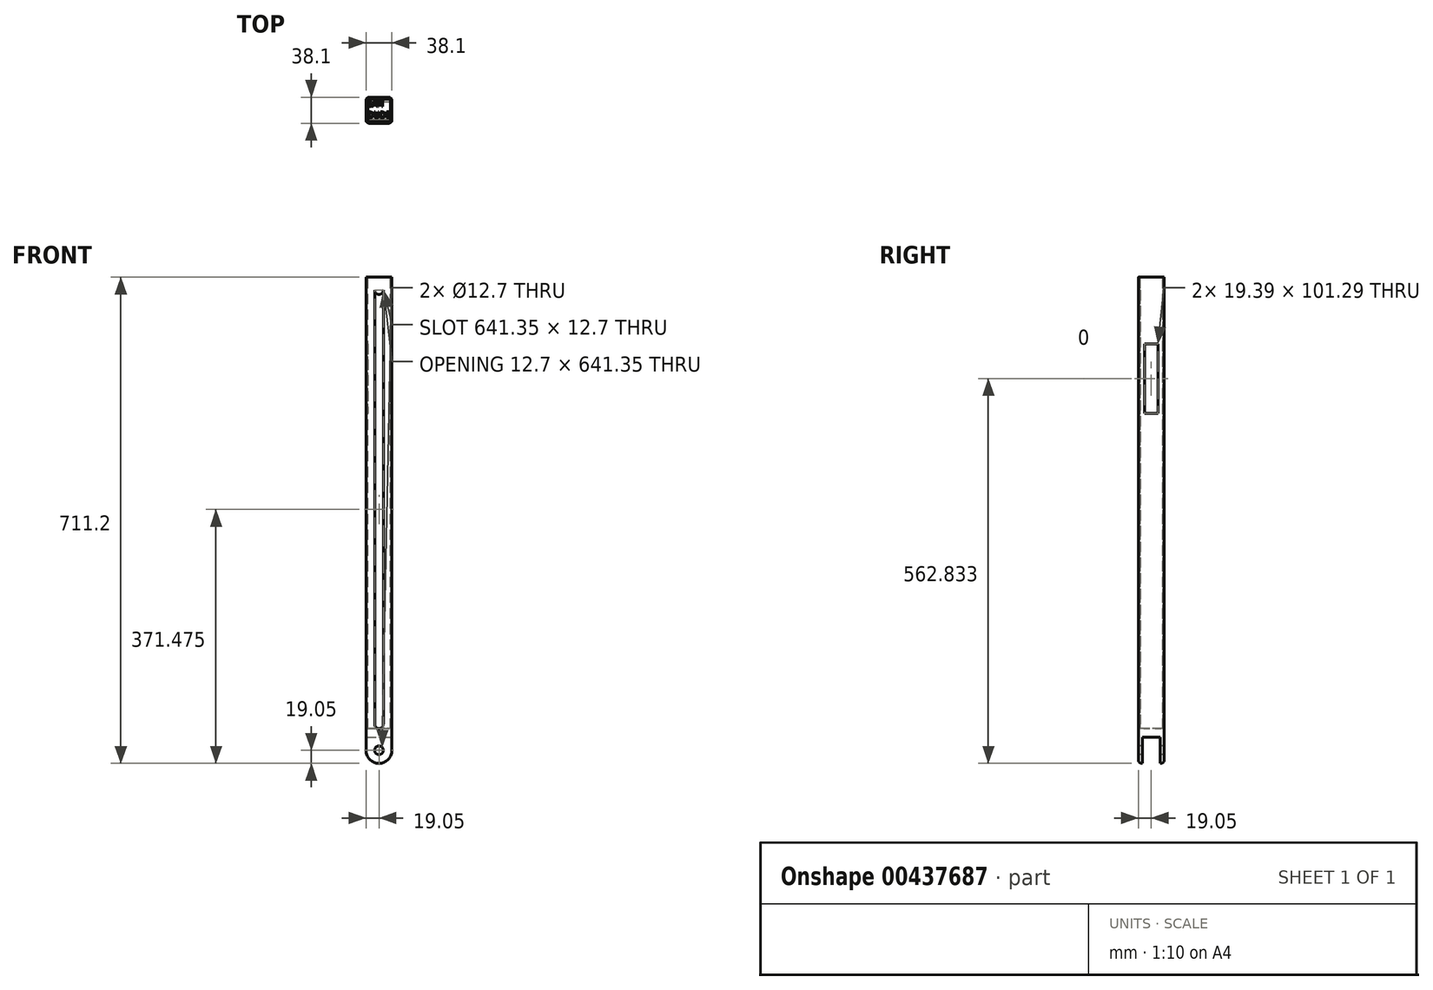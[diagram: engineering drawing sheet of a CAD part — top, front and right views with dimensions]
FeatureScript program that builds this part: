
annotation { "Feature Type Name" : "Feature", "Feature Type Description" : "" }
export const myFeature = defineFeature(function(context is Context, id is Id, definition is map)
    precondition{}
    {
        {
            var Q0;
            Q0=qCreatedBy(makeId("Top.planeOp"),FACE);
            var sketch = newSketch(context, id + "F0", { "sketchPlane" : qUnion([Q0])});
            skLineSegment(sketch, "E0.bottom", {"start": v(-19.05, 19.05) * mm, "end": v(19.05, 19.05) * mm});
            skLineSegment(sketch, "E0.top", {"start": v(-19.05, -19.05) * mm, "end": v(19.05, -19.05) * mm});
            skLineSegment(sketch, "E0.left", {"start": v(-19.05, 19.05) * mm, "end": v(-19.05, -19.05) * mm});
            skLineSegment(sketch, "E0.right", {"start": v(19.05, 19.05) * mm, "end": v(19.05, -19.05) * mm});
            skPoint(sketch, "E0.middle", {"position": v(0, 0) * mm});
            skSolve(sketch);
        }
        {
            var Q0;
            Q0=makeQuery(id+"F0.imprint","IMPRINT",FACE,{"disambiguationData":[TD([[makeQuery(id+"F0.imprint","IMPRINT",EDGE,{"derivedFrom":sQuery(id+"F0.wireOp",EDGE,"E0.bottom")}),-1.0]])]});
            extrude(context, id + "F1", {"entities" : qUnion([Q0]), "depth" : 711.2 * mm});
        }
        {
            var Q0;
            Q0=makeQuery(id+"F1.opExtrude","CAP_FACE",FACE,{"disambiguationData":[OSD([sQuery(id+"F0.wireOp",EDGE,"E0.bottom"),sQuery(id+"F0.wireOp",EDGE,"E0.top"),sQuery(id+"F0.wireOp",EDGE,"E0.left"),sQuery(id+"F0.wireOp",EDGE,"E0.right")])],"isStart":false});
            var sketch = newSketch(context, id + "F2", { "sketchPlane" : qUnion([Q0])});
            skLineSegment(sketch, "E1", {"start": v(-19.05, 0) * mm, "end": v(19.05, 0) * mm});
            skLineSegment(sketch, "E2", {"start": v(0, 19.05) * mm, "end": v(0, -19.05) * mm});
            skLineSegment(sketch, "E3.bottom", {"start": v(-16.51, 16.51) * mm, "end": v(16.51, 16.51) * mm});
            skLineSegment(sketch, "E3.top", {"start": v(-16.51, -16.51) * mm, "end": v(16.51, -16.51) * mm});
            skLineSegment(sketch, "E3.left", {"start": v(-16.51, 16.51) * mm, "end": v(-16.51, -16.51) * mm});
            skLineSegment(sketch, "E3.right", {"start": v(16.51, 16.51) * mm, "end": v(16.51, -16.51) * mm});
            skPoint(sketch, "E3.middle", {"position": v(0, 0) * mm});
            skSolve(sketch);
        }
        {
            var Q0;
            {var subQ0=sQuery(id+"F2.wireOp",EDGE,"E3.left");var subQ1=sQuery(id+"F2.wireOp",EDGE,"E1");var subQ2=makeQuery(id+"F2.imprint","INTERSECT",VERTEX,{"derivedFrom":[subQ1,subQ0]});Q0=makeQuery(id+"F2.imprint","IMPRINT",FACE,{"disambiguationData":[TD([[makeQuery(id+"F2.imprint","IMPRINT",EDGE,{"disambiguationData":[TD([[subQ2,-1.0]])],"derivedFrom":subQ1}),1.0]])]});}
            var Q1;
            {var subQ0=sQuery(id+"F2.wireOp",EDGE,"E2");var subQ1=sQuery(id+"F2.wireOp",EDGE,"E1");var subQ2=makeQuery(id+"F2.imprint","INTERSECT",VERTEX,{"derivedFrom":[subQ1,subQ0]});Q1=makeQuery(id+"F2.imprint","IMPRINT",FACE,{"disambiguationData":[TD([[makeQuery(id+"F2.imprint","IMPRINT",EDGE,{"disambiguationData":[TD([[subQ2,-1.0]])],"derivedFrom":subQ1}),1.0]])]});}
            var Q2;
            {var subQ0=sQuery(id+"F2.wireOp",EDGE,"E2");var subQ1=sQuery(id+"F2.wireOp",EDGE,"E1");var subQ2=makeQuery(id+"F2.imprint","INTERSECT",VERTEX,{"derivedFrom":[subQ1,subQ0]});Q2=makeQuery(id+"F2.imprint","IMPRINT",FACE,{"disambiguationData":[TD([[makeQuery(id+"F2.imprint","IMPRINT",EDGE,{"disambiguationData":[TD([[subQ2,-1.0]])],"derivedFrom":subQ1}),-1.0]])]});}
            var Q3;
            {var subQ0=sQuery(id+"F2.wireOp",EDGE,"E3.left");var subQ1=sQuery(id+"F2.wireOp",EDGE,"E1");var subQ2=makeQuery(id+"F2.imprint","INTERSECT",VERTEX,{"derivedFrom":[subQ1,subQ0]});Q3=makeQuery(id+"F2.imprint","IMPRINT",FACE,{"disambiguationData":[TD([[makeQuery(id+"F2.imprint","IMPRINT",EDGE,{"disambiguationData":[TD([[subQ2,-1.0]])],"derivedFrom":subQ1}),-1.0]])]});}
            extrude(context, id + "F3", {"entities" : qUnion([Q0, Q1, Q2, Q3]), "operationType" : NewBodyOperationType.REMOVE, "oppositeDirection" : true, "depth" : 660.4 * mm});
        }
        {
            var Q0;
            Q0=makeQuery(id+"F1.opExtrude","SWEPT_FACE",FACE,{"disambiguationData":[OSD([sQuery(id+"F0.wireOp",EDGE,"E0.top")])]});
            var sketch = newSketch(context, id + "F4", { "sketchPlane" : qUnion([Q0])});
            skLineSegment(sketch, "E4", {"start": v(0, 711.2) * mm, "end": v(0, 0) * mm});
            skCircle(sketch, "E5", {"center": v(0, 692.15) * mm, "radius": 6.35 * mm});
            skCircle(sketch, "E6", {"center": v(0, 57.15) * mm, "radius": 6.35 * mm});
            skLineSegment(sketch, "E7", {"start": v(-6.35, 692.15) * mm, "end": v(-6.35, 57.15) * mm});
            skLineSegment(sketch, "E8", {"start": v(6.35, 692.15) * mm, "end": v(6.35, 57.15) * mm});
            skSolve(sketch);
        }
        {
            var Q0;
            {var subQ5=sQuery(id+"F4.wireOp",EDGE,"E7");Q0=makeQuery(id+"F4.imprint","IMPRINT",FACE,{"disambiguationData":[TD([[makeQuery(id+"F4.imprint","IMPRINT",EDGE,{"derivedFrom":subQ5}),1.0]])]});}
            var Q1;
            {var subQ5=sQuery(id+"F4.wireOp",EDGE,"E8");Q1=makeQuery(id+"F4.imprint","IMPRINT",FACE,{"disambiguationData":[TD([[makeQuery(id+"F4.imprint","IMPRINT",EDGE,{"derivedFrom":subQ5}),-1.0]])]});}
            var Q2;
            {var subQ0=sQuery(id+"F4.wireOp",EDGE,"E5");var subQ1=sQuery(id+"F4.wireOp",EDGE,"E4");var subQ2=makeQuery(id+"F4.imprint","INTERSECT",VERTEX,{"disambiguationData":[OD(0.0)],"derivedFrom":[subQ1,subQ0]});Q2=makeQuery(id+"F4.imprint","IMPRINT",FACE,{"disambiguationData":[TD([[makeQuery(id+"F4.imprint","IMPRINT",EDGE,{"disambiguationData":[TD([[subQ2,-1.0]])],"derivedFrom":subQ1}),1.0]])]});}
            var Q3;
            {var subQ0=sQuery(id+"F4.wireOp",EDGE,"E5");var subQ1=sQuery(id+"F4.wireOp",EDGE,"E4");var subQ2=makeQuery(id+"F4.imprint","INTERSECT",VERTEX,{"disambiguationData":[OD(0.0)],"derivedFrom":[subQ1,subQ0]});Q3=makeQuery(id+"F4.imprint","IMPRINT",FACE,{"disambiguationData":[TD([[makeQuery(id+"F4.imprint","IMPRINT",EDGE,{"disambiguationData":[TD([[subQ2,-1.0]])],"derivedFrom":subQ1}),-1.0]])]});}
            var Q4;
            {var subQ0=sQuery(id+"F4.wireOp",EDGE,"E6");var subQ1=sQuery(id+"F4.wireOp",EDGE,"E4");var subQ2=makeQuery(id+"F4.imprint","INTERSECT",VERTEX,{"disambiguationData":[OD(0.0)],"derivedFrom":[subQ1,subQ0]});Q4=makeQuery(id+"F4.imprint","IMPRINT",FACE,{"disambiguationData":[TD([[makeQuery(id+"F4.imprint","IMPRINT",EDGE,{"disambiguationData":[TD([[subQ2,-1.0]])],"derivedFrom":subQ1}),-1.0]])]});}
            var Q5;
            {var subQ0=sQuery(id+"F4.wireOp",EDGE,"E6");var subQ1=sQuery(id+"F4.wireOp",EDGE,"E4");var subQ2=makeQuery(id+"F4.imprint","INTERSECT",VERTEX,{"disambiguationData":[OD(0.0)],"derivedFrom":[subQ1,subQ0]});Q5=makeQuery(id+"F4.imprint","IMPRINT",FACE,{"disambiguationData":[TD([[makeQuery(id+"F4.imprint","IMPRINT",EDGE,{"disambiguationData":[TD([[subQ2,-1.0]])],"derivedFrom":subQ1}),1.0]])]});}
            extrude(context, id + "F5", {"entities" : qUnion([Q0, Q1, Q2, Q3, Q4, Q5]), "operationType" : NewBodyOperationType.REMOVE, "oppositeDirection" : true, "depth" : 102.1 * mm});
        }
        {
            var Q0;
            Q0=makeQuery(id+"F1.opExtrude","SWEPT_FACE",FACE,{"disambiguationData":[OSD([sQuery(id+"F0.wireOp",EDGE,"E0.right")])]});
            var sketch = newSketch(context, id + "F6", { "sketchPlane" : qUnion([Q0])});
            skLineSegment(sketch, "E9.bottom", {"start": v(12.7, 38.1) * mm, "end": v(-12.7, 38.1) * mm});
            skLineSegment(sketch, "E9.top", {"start": v(12.7, -38.1) * mm, "end": v(-12.7, -38.1) * mm});
            skLineSegment(sketch, "E9.left", {"start": v(12.7, 38.1) * mm, "end": v(12.7, -38.1) * mm});
            skLineSegment(sketch, "E9.right", {"start": v(-12.7, 38.1) * mm, "end": v(-12.7, -38.1) * mm});
            skPoint(sketch, "E9.middle", {"position": v(0, 0) * mm});
            skSolve(sketch);
        }
        {
            var Q0;
            {var subQ0=sQuery(id+"F6.wireOp",EDGE,"E9.bottom");Q0=makeQuery(id+"F6.imprint","IMPRINT",FACE,{"disambiguationData":[TD([[makeQuery(id+"F6.imprint","IMPRINT",EDGE,{"derivedFrom":subQ0}),1.0]])]});}
            extrude(context, id + "F7", {"entities" : qUnion([Q0]), "operationType" : NewBodyOperationType.REMOVE, "oppositeDirection" : true, "depth" : 55.12 * mm});
        }
        {
            var Q0;
            {var subQ0=sQuery(id+"F0.wireOp",EDGE,"E0.right");var subQ1=sQuery(id+"F0.wireOp",EDGE,"E0.top");Q0=makeQuery(id+"F7.boolean.opBoolean","SPLIT",EDGE,{"disambiguationData":[TD([makeQuery(id+"F1.opExtrude","SWEPT_FACE",FACE,{"disambiguationData":[OSD([subQ1])]})])],"derivedFrom":makeQuery(id+"F1.opExtrude","CAP_EDGE",EDGE,{"disambiguationData":[OSD([subQ0])],"isStart":true})});}
            var Q1;
            {var subQ0=sQuery(id+"F0.wireOp",EDGE,"E0.bottom");var subQ1=sQuery(id+"F0.wireOp",EDGE,"E0.right");Q1=makeQuery(id+"F7.boolean.opBoolean","SPLIT",EDGE,{"disambiguationData":[TD([makeQuery(id+"F1.opExtrude","SWEPT_FACE",FACE,{"disambiguationData":[OSD([subQ0])]})])],"derivedFrom":makeQuery(id+"F1.opExtrude","CAP_EDGE",EDGE,{"disambiguationData":[OSD([subQ1])],"isStart":true})});}
            var Q2;
            {var subQ0=sQuery(id+"F0.wireOp",EDGE,"E0.left");var subQ1=sQuery(id+"F0.wireOp",EDGE,"E0.top");Q2=makeQuery(id+"F7.boolean.opBoolean","SPLIT",EDGE,{"disambiguationData":[TD([makeQuery(id+"F1.opExtrude","SWEPT_FACE",FACE,{"disambiguationData":[OSD([subQ1])]})])],"derivedFrom":makeQuery(id+"F1.opExtrude","CAP_EDGE",EDGE,{"disambiguationData":[OSD([subQ0])],"isStart":true})});}
            var Q3;
            {var subQ0=sQuery(id+"F0.wireOp",EDGE,"E0.bottom");var subQ1=sQuery(id+"F0.wireOp",EDGE,"E0.left");Q3=makeQuery(id+"F7.boolean.opBoolean","SPLIT",EDGE,{"disambiguationData":[TD([makeQuery(id+"F1.opExtrude","SWEPT_FACE",FACE,{"disambiguationData":[OSD([subQ0])]})])],"derivedFrom":makeQuery(id+"F1.opExtrude","CAP_EDGE",EDGE,{"disambiguationData":[OSD([subQ1])],"isStart":true})});}
            fillet(context, id + "F8", {"entities" : qUnion([Q0, Q1, Q2, Q3]), "radius" : 19.05 * mm, "tangentPropagation" : true, "allowEdgeOverflow" : false});
        }
        {
            var Q0;
            Q0=makeQuery(id+"F1.opExtrude","SWEPT_FACE",FACE,{"disambiguationData":[OSD([sQuery(id+"F0.wireOp",EDGE,"E0.top")])]});
            var sketch = newSketch(context, id + "F9", { "sketchPlane" : qUnion([Q0])});
            skCircle(sketch, "E10", {"center": v(0, 19.05) * mm, "radius": 6.35 * mm});
            skSolve(sketch);
        }
        {
            var Q0;
            Q0=makeQuery(id+"F9.imprint","IMPRINT",FACE,{"disambiguationData":[TD([[makeQuery(id+"F9.imprint","IMPRINT",EDGE,{"derivedFrom":sQuery(id+"F9.wireOp",EDGE,"E10")}),1.0]])]});
            extrude(context, id + "F10", {"entities" : qUnion([Q0]), "operationType" : NewBodyOperationType.REMOVE, "oppositeDirection" : true, "depth" : 54.36 * mm});
        }
        {
            var Q0;
            Q0=makeQuery(id+"F1.opExtrude","SWEPT_FACE",FACE,{"disambiguationData":[OSD([sQuery(id+"F0.wireOp",EDGE,"E0.right")])]});
            var sketch = newSketch(context, id + "F11", { "sketchPlane" : qUnion([Q0])});
            skLineSegment(sketch, "E11.bottom", {"start": v(-9.7, 512.19) * mm, "end": v(9.7, 512.19) * mm});
            skLineSegment(sketch, "E11.top", {"start": v(-9.7, 910.21) * mm, "end": v(9.7, 910.21) * mm});
            skLineSegment(sketch, "E11.left", {"start": v(-9.7, 512.19) * mm, "end": v(-9.7, 910.21) * mm});
            skLineSegment(sketch, "E11.right", {"start": v(9.7, 512.19) * mm, "end": v(9.7, 910.21) * mm});
            skPoint(sketch, "E11.middle", {"position": v(0, 711.2) * mm});
            skLineSegment(sketch, "E12", {"start": v(-9.7, 613.48) * mm, "end": v(9.7, 613.48) * mm});
            skSolve(sketch);
        }
        {
            var Q0;
            {var subQ0=sQuery(id+"F11.wireOp",EDGE,"E11.bottom");Q0=makeQuery(id+"F11.imprint","IMPRINT",FACE,{"disambiguationData":[TD([[makeQuery(id+"F11.imprint","IMPRINT",EDGE,{"derivedFrom":subQ0}),1.0]])]});}
            extrude(context, id + "F12", {"entities" : qUnion([Q0]), "operationType" : NewBodyOperationType.REMOVE, "oppositeDirection" : true, "depth" : 118.36 * mm});
        }
        {
            var Q0;
            Q0=makeQuery(id+"F1.opExtrude","SWEPT_EDGE",EDGE,{"disambiguationData":[OSD([sQuery(id+"F0.wireOp",EDGE,"E0.top"),sQuery(id+"F0.wireOp",EDGE,"E0.right")])]});
            var Q1;
            Q1=makeQuery(id+"F1.opExtrude","SWEPT_EDGE",EDGE,{"disambiguationData":[OSD([sQuery(id+"F0.wireOp",EDGE,"E0.bottom"),sQuery(id+"F0.wireOp",EDGE,"E0.right")])]});
            fillet(context, id + "F13", {"entities" : qUnion([Q0, Q1]), "radius" : 5.08 * mm, "tangentPropagation" : true, "allowEdgeOverflow" : false});
        }
        {
            var Q0;
            Q0=makeQuery(id+"F3.boolean.opBoolean","COPY",FACE,{"derivedFrom":makeQuery(id+"F3.opExtrude","CAP_FACE",FACE,{"disambiguationData":[OSD([sQuery(id+"F2.wireOp",EDGE,"E3.bottom"),sQuery(id+"F2.wireOp",EDGE,"E3.top"),sQuery(id+"F2.wireOp",EDGE,"E3.left"),sQuery(id+"F2.wireOp",EDGE,"E3.right")])],"isStart":false})});
            var sketch = newSketch(context, id + "F14", { "sketchPlane" : qUnion([Q0])});
            skText(sketch, "E13", { "text": "SAH \nDUDE\n", "fontName": "OpenSans-Regular.ttf"});
            const initialGuessF14  = {"E13": [-0.01651, 0.00544, 1, 0, 0.00865]};
            skSetInitialGuess(sketch, initialGuessF14);
            skSolve(sketch);
        }
        {
            var Q0;
            Q0 = qSketchRegion(id + "F14", true);
            var Q1;
            Q1 = qSketchRegion(id + "F14", true);
            extrude(context, id + "F15", {"entities" : qUnion([Q0, Q1]), "operationType" : NewBodyOperationType.ADD, "depth" : 0.25 * mm});
        }
    });
